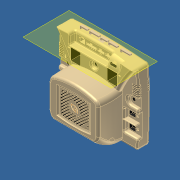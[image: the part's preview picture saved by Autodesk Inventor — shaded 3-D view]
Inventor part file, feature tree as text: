
AUTODESK INVENTOR PART (.ipt)
format: ipt  version: 2012 (Build 160160000, 160)  size: 3,483,648 bytes
history: native  units: in
note: dims shown in document units (in); Inventor stores cm internally (conversion verified against a paired STEP export)
features: sketch x47, extrude x43, fillet x43, projected_geometry x20, plane x6, hole x1, revolve x1, emboss x1
ambient origin geometry x8: Origin, YZ Plane, XZ Plane, XY Plane, X Axis, Y Axis, Z Axis, Center Point
bodies: Solid1 (feature_tree)
feature tree (162):
  extrude  "Extrusion3"  Depth=4.251in
  extrude  "Extrusion4"  Depth=0.0535in
  extrude  "Extrusion5"  Depth=0.72in
  extrude  "Extrusion6"  Depth=1.308in TaperAngle=0.0deg
  extrude  "Extrusion7"  Depth=0.052in
  extrude  "Extrusion9"  Depth=0.052in
  extrude  "Extrusion10"  Depth=1.308in TaperAngle=0.0deg
  extrude  "Extrusion11"  Depth=1.308in TaperAngle=0.0deg
  extrude  "Extrusion12"  Depth=0.218in TaperAngle=0.0deg
  extrude  "Extrusion13"  Depth=2.01in
  fillet  "Fillet1"  Radius=0.768in
  fillet  "Fillet3"  Radius=0.31in
  fillet  "Fillet4"  Radius=0.615in
  fillet  "Fillet5"  Radius=0.125in
  fillet  "Fillet6"  Radius=0.081in
  fillet  "Fillet7"  Radius=0.05in
  fillet  "Fillet8"  Radius=0.05in
  extrude  "Extrusion15"  Depth=0.036in
  fillet  "Fillet9"  Radius=0.05in
  fillet  "Fillet10"  Radius=0.4706in
  fillet  "Fillet11"  Radius=0.4706in
  fillet  "Fillet12"  Radius=0.218in
  fillet  "Fillet13"  Radius=0.15in
  fillet  "Fillet14"  Radius=0.15in
  fillet  "Fillet15"  Radius=0.15in
  plane  "Work Plane1"
  extrude  "Extrusion16"  Depth=0.15in
  fillet  "Fillet17"  Radius=0.15in
  fillet  "Fillet18"  Radius=0.15in
  fillet  "Fillet19"  [1 undecoded]
  fillet  "Fillet20"  Radius=5.0in
  fillet  "Fillet21"  Radius=0.3in
  fillet  "Fillet22"  Radius=0.3in
  fillet  "Fillet23"  Radius=0.272in
  extrude  "Extrusion17"  Depth=0.125in
  fillet  "Fillet24"  Radius=0.096in
  extrude  "Extrusion18"  Depth=0.054in TaperAngle=0.0deg
  extrude  "Extrusion19"  Depth=0.055in
  extrude  "Extrusion20"  Depth=0.055in
  plane  "Work Plane2"
  extrude  "Extrusion21"  Depth=0.055in
  extrude  "Extrusion22"  TaperAngle=90.0deg  [1 undecoded]
  fillet  "Fillet25"  Radius=0.05in
  extrude  "Extrusion23"  Depth=0.05in
  extrude  "Extrusion24"  Depth=0.05in
  extrude  "Extrusion25"  Depth=0.055in
  fillet  "Fillet26"  Radius=0.05in
  plane  "Work Plane3"
  extrude  "Extrusion26"  Depth=0.055in
  fillet  "Fillet27"  Radius=0.05in
  hole  "Hole1"  [1 undecoded]
  extrude  "Extrusion27"  Depth=0.05in
  fillet  "Fillet28"  Radius=0.055in
  fillet  "Fillet29"  [1 undecoded]
  fillet  "Fillet30"  [1 undecoded]
  fillet  "Fillet31"  [1 undecoded]
  fillet  "Fillet32"  Radius=0.05in
  fillet  "Fillet33"  Radius=0.055in
  fillet  "Fillet34"  Radius=0.055in
  fillet  "Fillet35"  Radius=0.055in
  plane  "Work Plane4"
  extrude  "Extrusion28"  TaperAngle=90.0deg  [1 undecoded]
  fillet  "Fillet36"  Radius=0.05in
  extrude  "Extrusion29"  TaperAngle=90.0deg  [1 undecoded]
  extrude  "Extrusion30"  Depth=0.055in
  extrude  "Extrusion31"  Depth=0.05in
  extrude  "Extrusion32"  TaperAngle=90.0deg  [1 undecoded]
  extrude  "Extrusion33"  TaperAngle=90.0deg  [1 undecoded]
  extrude  "Extrusion34"  Depth=0.055in
  revolve  "Revolution1"  [1 undecoded]
  extrude  "Extrusion35"  Depth=0.05in
  extrude  "Extrusion36"  Depth=0.08in
  plane  "Work Plane5"
  emboss  "Emboss1"
  sketch  "Sketch38"  dims[d135=0.615in d138=0.524in]
  extrude  "Extrusion39"  Depth=0.84in TaperAngle=0.0deg
  fillet  "Fillet38"  Radius=0.524in
  plane  "Work Plane9"
  extrude  "Extrusion40"  Depth=0.524in
  extrude  "Extrusion41"  Depth=0.647in TaperAngle=0.0deg
  fillet  "Fillet39"  Radius=0.22in
  extrude  "Extrusion42"  Depth=0.219in
  extrude  "Extrusion43"  Depth=0.1in
  fillet  "Fillet40"  Radius=0.058in
  extrude  "Extrusion44"  Depth=0.056in
  extrude  "Extrusion45"  Depth=0.1in
  fillet  "Fillet41"  Radius=0.1in
  extrude  "Extrusion46"  Depth=0.13in
  extrude  "Extrusion47"  Depth=0.357in
  fillet  "Fillet42"  Radius=0.334in
  extrude  "Extrusion48"  Depth=1.1875in
  extrude  "Extrusion49"  Depth=0.344in
  fillet  "Fillet43"  Radius=0.489in
  fillet  "Fillet44"  Radius=0.337in
  fillet  "Fillet45"  Radius=0.25in
  fillet  "Fillet46"  Radius=0.143in
  sketch  "Sketch1"  dims[d0=3.876in d1=4.251in]
  sketch  "Sketch2"  dims[d5=0.0535in d6=0.0535in]
  sketch  "Sketch3"  dims[d9=2.005in d10=0.0in d11=0.72in]
  sketch  "Sketch4"  dims[d12=0.72in d13=1.308in d14=0.0in]
  sketch  "Sketch5"  dims[d15=0.052in d16=0.052in]
  sketch  "Sketch6"  dims[d17=0.052in d18=0.052in]
  sketch  "Sketch7"  dims[d19=2.475in d20=0.0in d21=1.308in d22=0.0in]
  sketch  "Sketch8"  dims[d23=1.308in d24=0.0in d27=1.308in d28=0.0in]
  sketch  "Sketch9"  dims[d29=1.308in d30=0.0in d31=0.218in d32=0.0in]
  sketch  "Sketch10"  dims[d34=0.543in d35=2.01in d36=0.768in d37=0.31in d38=0.0in d39=0.615in d40=0.0in d41=0.125in d43=0.081in d44=0.05in d45=0.05in]
  sketch  "Sketch11"  dims[d46=0.05in d47=0.036in d48=0.05in d51=0.4706in d52=0.4706in d53=0.218in d54=0.0in d55=0.15in d56=0.15in d57=0.15in]
  sketch  "Sketch12"  dims[d58=0.078in d59=0.15in d60=0.15in d61=0.15in d62=-0.6875in d63=5.0in d64=0.0in d66=0.3in d67=0.3in d68=0.272in]
  sketch  "Sketch13"  dims[d69=0.409in d70=0.125in d71=0.096in]
  sketch  "Sketch14"  dims[d72=0.125in d74=0.054in d75=0.0in]
  sketch  "Sketch15"  dims[d76=0.125in d77=0.055in]
  sketch  "Sketch16"  dims[d78=0.055in d79=0.055in]
  sketch  "Sketch17"  dims[d80=0.055in d81=0.055in]
  sketch  "Sketch18"  dims[d82=90.0deg d83=90.0deg d84=0.05in]
  sketch  "Sketch19"  dims[d85=0.05in d86=0.05in]
  projected_geometry  "Projected Loop1"
  sketch  "Sketch20"  dims[d88=0.05in d89=0.05in]
  sketch  "Sketch21"  dims[d90=0.055in d91=0.055in d92=0.05in]
  sketch  "Sketch22"  dims[d93=0.05in d94=0.055in d95=0.05in]
  projected_geometry  "Projected Loop2"
  projected_geometry  "Projected Loop3"
  projected_geometry  "Projected Loop4"
  projected_geometry  "Projected Loop5"
  projected_geometry  "Projected Loop6"
  projected_geometry  "Projected Loop7"
  projected_geometry  "Projected Loop8"
  projected_geometry  "Projected Loop9"
  sketch  "Sketch23"  dims[d96=0.055in d97=90.0deg]
  sketch  "Sketch24"  dims[d98=90.0deg d99=0.05in d100=0.055in d101=90.0deg d102=90.0deg d103=90.0deg d104=0.05in d105=0.055in d106=0.055in d107=0.055in]
  projected_geometry  "Projected Loop10"
  projected_geometry  "Projected Loop11"
  sketch  "Sketch26"  dims[d108=0.05in d109=90.0deg d110=0.05in]
  projected_geometry  "Projected Loop19"
  projected_geometry  "Projected Loop20"
  projected_geometry  "Projected Loop21"
  projected_geometry  "Projected Loop22"
  projected_geometry  "Projected Loop23"
  projected_geometry  "Projected Loop24"
  projected_geometry  "Projected Loop25"
  sketch  "Sketch27"  dims[d111=0.055in d112=90.0deg]
  sketch  "Sketch28"  dims[d113=0.05in d114=0.055in]
  sketch  "Sketch29"  dims[d115=0.055in d116=0.05in]
  sketch  "Sketch30"  dims[d117=0.05in d118=90.0deg]
  sketch  "Sketch31"  dims[d119=90.0deg d120=90.0deg]
  projected_geometry  "Projected Loop26"
  sketch  "Sketch32"  dims[d121=0.05in d123=0.055in]
  sketch  "Sketch33"  dims[d124=90.0deg d125=0.055in]
  sketch  "Sketch34"  dims[d126=0.05in d127=0.05in]
  sketch  "Sketch35"  dims[d128=0.055in d129=0.08in]
  projected_geometry  "Projected Loop27"
  sketch  "Sketch36"  dims[d130=0.08in d131=0.84in d132=0.0in d134=0.524in]
  sketch  "Sketch39"  dims[d139=0.615in d140=0.647in d141=0.0in d142=0.22in]
  sketch  "Sketch40"  dims[d143=0.255in d144=0.219in]
  sketch  "Sketch41"  dims[d145=0.083in d146=0.1in d147=0.058in]
  sketch  "Sketch42"  dims[d148=0.549in d149=0.056in]
  sketch  "Sketch43"  dims[d150=0.056in d151=0.1in d152=0.1in]
  sketch  "Sketch44"  dims[d153=0.13in d154=0.13in]
  sketch  "Sketch45"  dims[d155=0.13in d156=0.357in d157=0.334in]
  sketch  "Sketch46"  dims[d158=0.248in d159=0.0in d160=1.1875in]
  sketch  "Sketch47"  dims[d161=0.114in d162=0.344in d163=0.489in d164=0.0in d165=0.337in d166=0.25in d167=0.143in d168=0.0in]
  sketch  "Sketch48"  dims[d169=0.066in]
  sketch  "Sketch49"  dims[d170=0.431in d171=0.51in d172=0.51in d173=0.068in d174=0.067in d175=0.067in d176=0.234in d177=0.0in d178=0.282in d179=0.422in d180=0.446in d181=0.167in d182=0.0in d183=0.141in d184=0.04in d185=0.04in d186=0.04in d187=0.04in d190=0.04in d191=0.04in d192=0.04in d193=0.062in d194=0.0in d195=0.0in d196=0.0in d197=0.04in d198=0.04in d199=0.04in d200=0.04in d201=0.0in d202=0.0in d203=0.04in d204=0.04in d205=0.0in d206=7.0in d207=0.0in d208=0.02in d209=3.4375in d210=0.17in d211=0.17in d212=0.5in d213=0.0in d214=0.02in d215=0.174in d216=0.5in d217=0.375in d218=0.25in d219=0.5635in d220=0.745in d221=0.8108in d222=0.618in d223=0.234in d224=0.0in d225=0.08in d226=0.08in d227=0.08in d228=0.08in d229=0.08in d230=0.08in d231=0.035in d232=0.035in d233=0.068in d234=0.51in d235=0.067in d236=0.067in d237=0.51in d238=0.618in d239=0.446in d240=0.141in d241=0.04in d243=0.04in d245=0.04in d246=0.04in d247=0.04in d248=0.062in d249=0.0in d250=0.0in d251=0.04in d252=0.04in d253=0.0in d254=0.04in d255=0.04in d256=0.0in d257=0.04in d258=0.04in d259=0.0in d261=0.04in d262=0.0in d263=0.04in d264=-1.4375in d265=0.167in d266=0.167in d267=0.5in d268=0.0in d269=0.02in d270=0.0001in d271=0.0in d272=0.0001in d273=0.0in d274=0.055in d275=0.207in d276=0.3in d277=0.0in d278=0.0001in d279=0.0in d280=0.34in d281=0.335in d282=0.123in d283=0.34in d284=0.335in d285=0.123in d286=0.068in d287=0.068in d288=0.161in d289=0.0in d290=0.335in d291=0.335in d292=0.34in d293=0.34in d294=0.068in d295=0.068in d296=0.123in d297=0.123in d298=0.0in d299=0.0in d300=90.0deg d301=0.066in d302=0.066in d303=0.033in d304=0.033in d305=0.033in d306=0.066in d307=0.066in d308=0.066in d309=0.066in d310=0.05in d311=0.05in d312=0.05in d313=0.0in d314=0.01in d315=0.01in d316=0.01in d317=0.033in d318=0.033in d319=0.033in d320=0.033in d321=0.033in d322=0.033in d323=0.0001in d324=0.0in d325=3.9375in d335=0.0001in d336=0.0in d338=0.2in d340=0.03in d341=0.03in d342=0.03in d346=0.01in d347=0.0in d351=0.03in d352=0.03in d354=0.01in d355=3.875in d356=0.07in d357=0.106in d358=0.07in d359=0.106in d360=0.534in d361=0.07in d362=0.106in d363=0.4in d364=0.07in d365=0.106in d366=0.294in d367=0.07in d368=0.106in d369=0.546in d370=0.136in d371=0.0in d372=0.07in d373=0.315in d374=0.0in d375=0.035in d376=0.07in d377=0.511in d378=0.28in d379=0.0in d380=0.07in d381=0.453in d382=0.0in d383=0.035in d384=0.07in d385=0.43in d386=0.27in d387=0.0in d388=0.07in d389=0.345in d390=0.0in d391=0.035in d392=0.07in d393=0.358in d394=0.27in d395=0.0in d396=0.07in d397=0.4in d398=0.0in d399=0.035in d400=0.07in d401=0.555in d402=0.25in d403=0.0in d404=0.07in d405=0.473in d406=0.0in d407=0.035in d408=0.035in d409=0.035in d410=0.01in]
note: 11 required parameter values undecoded (feature->parameter linkage not recoverable at this tier; creation-order binding heuristic only, values carry confidence <= 0.55)